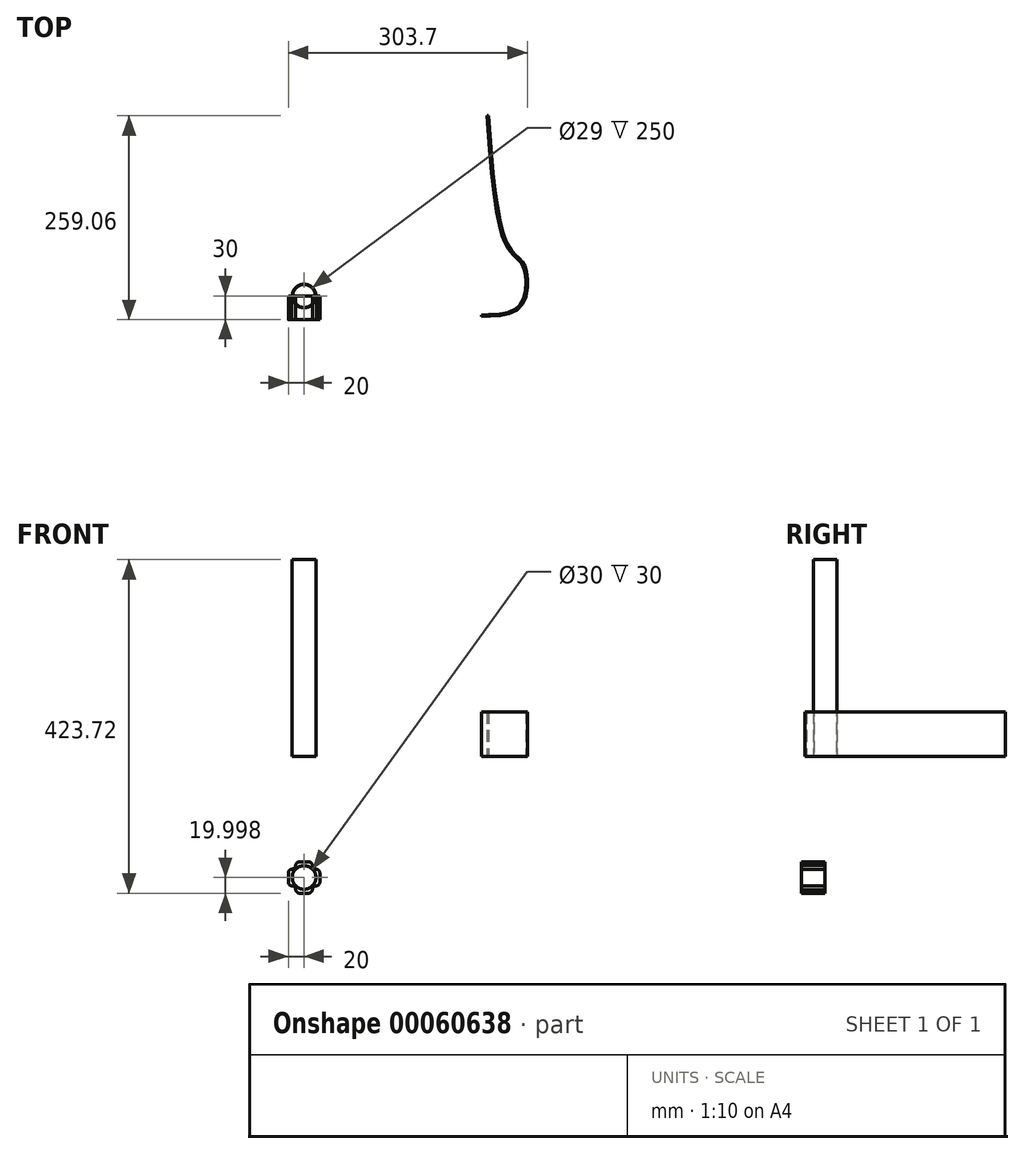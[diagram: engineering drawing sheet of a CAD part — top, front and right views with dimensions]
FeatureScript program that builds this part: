
annotation { "Feature Type Name" : "Feature", "Feature Type Description" : "" }
export const myFeature = defineFeature(function(context is Context, id is Id, definition is map)
    precondition{}
    {
        {
            var Q0;
            Q0=qCreatedBy(makeId("Top.planeOp"),FACE);
            var sketch = newSketch(context, id + "F0", { "sketchPlane" : qUnion([Q0])});
            skCircle(sketch, "E0", {"center": v(0, 0) * mm, "radius": 15 * mm});
            skCircle(sketch, "E1", {"center": v(0, 0) * mm, "radius": 14.5 * mm});
            skSolve(sketch);
        }
        {
            var Q0;
            Q0 = qSketchRegion(id + "F0", true);
            extrude(context, id + "F1", {"entities" : qUnion([Q0]), "depth" : 250 * mm});
        }
        {
            var Q0;
            Q0=qCreatedBy(makeId("Front.planeOp"),FACE);
            var sketch = newSketch(context, id + "F2", { "sketchPlane" : qUnion([Q0])});
            skCircle(sketch, "E2", {"center": v(0, -153.72) * mm, "radius": 15 * mm});
            skLineSegment(sketch, "E3.0", {"start": v(-5.6, -133.72) * mm, "end": v(5.6, -133.72) * mm});
            skLineSegment(sketch, "E3.1", {"start": v(20, -148.12) * mm, "end": v(20, -159.33) * mm});
            skLineSegment(sketch, "E3.2", {"start": v(5.6, -173.72) * mm, "end": v(-5.6, -173.72) * mm});
            skLineSegment(sketch, "E3.3", {"start": v(-20, -159.33) * mm, "end": v(-20, -148.12) * mm});
            skPoint(sketch, "E3.0.midPoint", {"position": v(0, -133.72) * mm});
            skPoint(sketch, "E4", {"position": v(20, -153.72) * mm});
            skLineSegment(sketch, "E5", {"start": v(20, -133.72) * mm, "end": v(-20, -173.72) * mm, "construction": true});
            skLineSegment(sketch, "E6", {"start": v(20, -173.72) * mm, "end": v(-20, -133.72) * mm, "construction": true});
            skPoint(sketch, "E7", {"position": v(10.6, -143.12) * mm});
            skPoint(sketch, "E8", {"position": v(-10.6, -164.33) * mm});
            skPoint(sketch, "E9", {"position": v(10.6, -164.33) * mm});
            skPoint(sketch, "E10", {"position": v(-10.6, -143.12) * mm});
            skLineSegment(sketch, "E11.top", {"start": v(15.6, -143.12) * mm, "end": v(15, -143.12) * mm});
            skLineSegment(sketch, "E11.right", {"start": v(10.6, -138.12) * mm, "end": v(10.6, -138.72) * mm});
            skLineSegment(sketch, "E12.top", {"start": v(15.6, -164.33) * mm, "end": v(15, -164.33) * mm});
            skLineSegment(sketch, "E12.right", {"start": v(10.6, -169.33) * mm, "end": v(10.6, -168.72) * mm});
            skLineSegment(sketch, "E13.top", {"start": v(-15.6, -164.33) * mm, "end": v(-15, -164.33) * mm});
            skLineSegment(sketch, "E13.right", {"start": v(-10.6, -169.33) * mm, "end": v(-10.6, -168.72) * mm});
            skLineSegment(sketch, "E14.top", {"start": v(-15.6, -143.12) * mm, "end": v(-15, -143.12) * mm});
            skLineSegment(sketch, "E14.right", {"start": v(-10.6, -138.12) * mm, "end": v(-10.6, -138.72) * mm});
            skArc(sketch, "E15.filletArc", {"start": v(-10.6, -169.33) * mm, "mid": v(-12.07, -165.8) * mm, "end": v(-15.6, -164.33) * mm});
            skArc(sketch, "E16.filletArc", {"start": v(-15.6, -143.12) * mm, "mid": v(-12.07, -141.65) * mm, "end": v(-10.6, -138.12) * mm});
            skArc(sketch, "E17.filletArc", {"start": v(10.6, -138.12) * mm, "mid": v(12.07, -141.65) * mm, "end": v(15.6, -143.12) * mm});
            skArc(sketch, "E18.filletArc", {"start": v(15.6, -164.33) * mm, "mid": v(12.07, -165.8) * mm, "end": v(10.6, -169.33) * mm});
            skPoint(sketch, "E19.visualSharp", {"position": v(20, -164.33) * mm});
            skArc(sketch, "E19.filletArc", {"start": v(15, -164.33) * mm, "mid": v(18.54, -162.86) * mm, "end": v(20, -159.33) * mm});
            skPoint(sketch, "E20.visualSharp", {"position": v(20, -143.12) * mm});
            skArc(sketch, "E20.filletArc", {"start": v(20, -148.12) * mm, "mid": v(18.54, -144.58) * mm, "end": v(15, -143.12) * mm});
            skPoint(sketch, "E21.visualSharp", {"position": v(10.6, -133.72) * mm});
            skArc(sketch, "E21.filletArc", {"start": v(10.6, -138.72) * mm, "mid": v(9.14, -135.19) * mm, "end": v(5.6, -133.72) * mm});
            skPoint(sketch, "E22.visualSharp", {"position": v(-10.6, -133.72) * mm});
            skArc(sketch, "E22.filletArc", {"start": v(-5.6, -133.72) * mm, "mid": v(-9.14, -135.19) * mm, "end": v(-10.6, -138.72) * mm});
            skPoint(sketch, "E23.visualSharp", {"position": v(-20, -143.12) * mm});
            skArc(sketch, "E23.filletArc", {"start": v(-15, -143.12) * mm, "mid": v(-18.54, -144.58) * mm, "end": v(-20, -148.12) * mm});
            skPoint(sketch, "E24.visualSharp", {"position": v(-20, -164.33) * mm});
            skArc(sketch, "E24.filletArc", {"start": v(-20, -159.33) * mm, "mid": v(-18.54, -162.86) * mm, "end": v(-15, -164.33) * mm});
            skPoint(sketch, "E25.visualSharp", {"position": v(-10.6, -173.72) * mm});
            skArc(sketch, "E25.filletArc", {"start": v(-10.6, -168.72) * mm, "mid": v(-9.14, -172.26) * mm, "end": v(-5.6, -173.72) * mm});
            skPoint(sketch, "E26.visualSharp", {"position": v(10.6, -173.72) * mm});
            skArc(sketch, "E26.filletArc", {"start": v(5.6, -173.72) * mm, "mid": v(9.14, -172.26) * mm, "end": v(10.6, -168.72) * mm});
            skSolve(sketch);
        }
        {
            var Q0;
            Q0 = qSketchRegion(id + "F2", true);
            extrude(context, id + "F3", {"entities" : qUnion([Q0]), "depth" : 30 * mm});
        }
        {
            var Q0;
            Q0=qCreatedBy(makeId("Top.planeOp"),FACE);
            var sketch = newSketch(context, id + "F4", { "sketchPlane" : qUnion([Q0])});
            skLineSegment(sketch, "E27", {"start": v(195.56, 229.06) * mm, "end": v(195.56, -25.94) * mm, "construction": true});
            skLineSegment(sketch, "E28", {"start": v(225.56, 229.06) * mm, "end": v(225.56, -25.94) * mm});
            skFitSpline(sketch, "E29", {"points": [v(234.4, 229.06) * mm, v(258.34, 65.82) * mm, v(275.52, 45.77) * mm, v(282.68, 29.07) * mm, v(274.56, -14.36) * mm, v(225.56, -25.94) * mm, v(195.56, -25.94) * mm], "startDerivative": vector(48.25, -659.53) * mm, "endDerivative": vector(-199.67, 0.53) * mm});
            skFitSpline(sketch, "E30.0", {"points": [v(232.41, 228.92) * mm, v(233.42, 215.18) * mm, v(235.43, 187.69) * mm, v(238.89, 148.44) * mm, v(242.52, 119.07) * mm, v(246.1, 98.57) * mm, v(248.66, 87.2) * mm, v(250.95, 79.09) * mm, v(252.8, 73.53) * mm, v(254.45, 69.35) * mm, v(255.85, 66.29) * mm, v(257.3, 63.42) * mm, v(259.22, 60.23) * mm, v(262.4, 55.84) * mm, v(265.63, 52.37) * mm, v(268.7, 49.5) * mm, v(270.85, 47.55) * mm, v(272.47, 46.05) * mm, v(273.63, 44.87) * mm, v(274.7, 43.7) * mm, v(275.9, 42.2) * mm, v(277.54, 39.67) * mm, v(278.84, 36.73) * mm, v(279.87, 33.11) * mm, v(280.42, 30.5) * mm, v(280.8, 28.19) * mm, v(281.14, 25.71) * mm, v(281.48, 22.38) * mm, v(281.71, 18.09) * mm, v(281.7, 12.12) * mm, v(281.16, 5.99) * mm, v(279.92, 0.12) * mm, v(278.6, -4.05) * mm, v(276.87, -7.88) * mm, v(275.06, -10.72) * mm, v(273.38, -12.74) * mm, v(271.54, -14.57) * mm, v(268.9, -16.59) * mm, v(265.24, -18.59) * mm, v(259.81, -20.74) * mm, v(252.19, -22.53) * mm, v(244, -23.42) * mm, v(237.46, -23.76) * mm, v(232.63, -23.89) * mm, v(228.74, -23.93) * mm, v(225.75, -23.94) * mm, v(222.85, -23.95) * mm, v(219.41, -23.96) * mm, v(214.25, -23.97) * mm, v(208.33, -23.97) * mm, v(201.8, -23.96) * mm, v(197.65, -23.94) * mm, v(195.57, -23.94) * mm]});
            skLineSegment(sketch, "E31", {"start": v(232.41, 228.92) * mm, "end": v(234.4, 229.06) * mm});
            skSolve(sketch);
        }
        {
            var Q0;
            Q0 = qSketchRegion(id + "F4", true);
            extrude(context, id + "F5", {"entities" : qUnion([Q0]), "depth" : 56.47 * mm});
        }
    });
